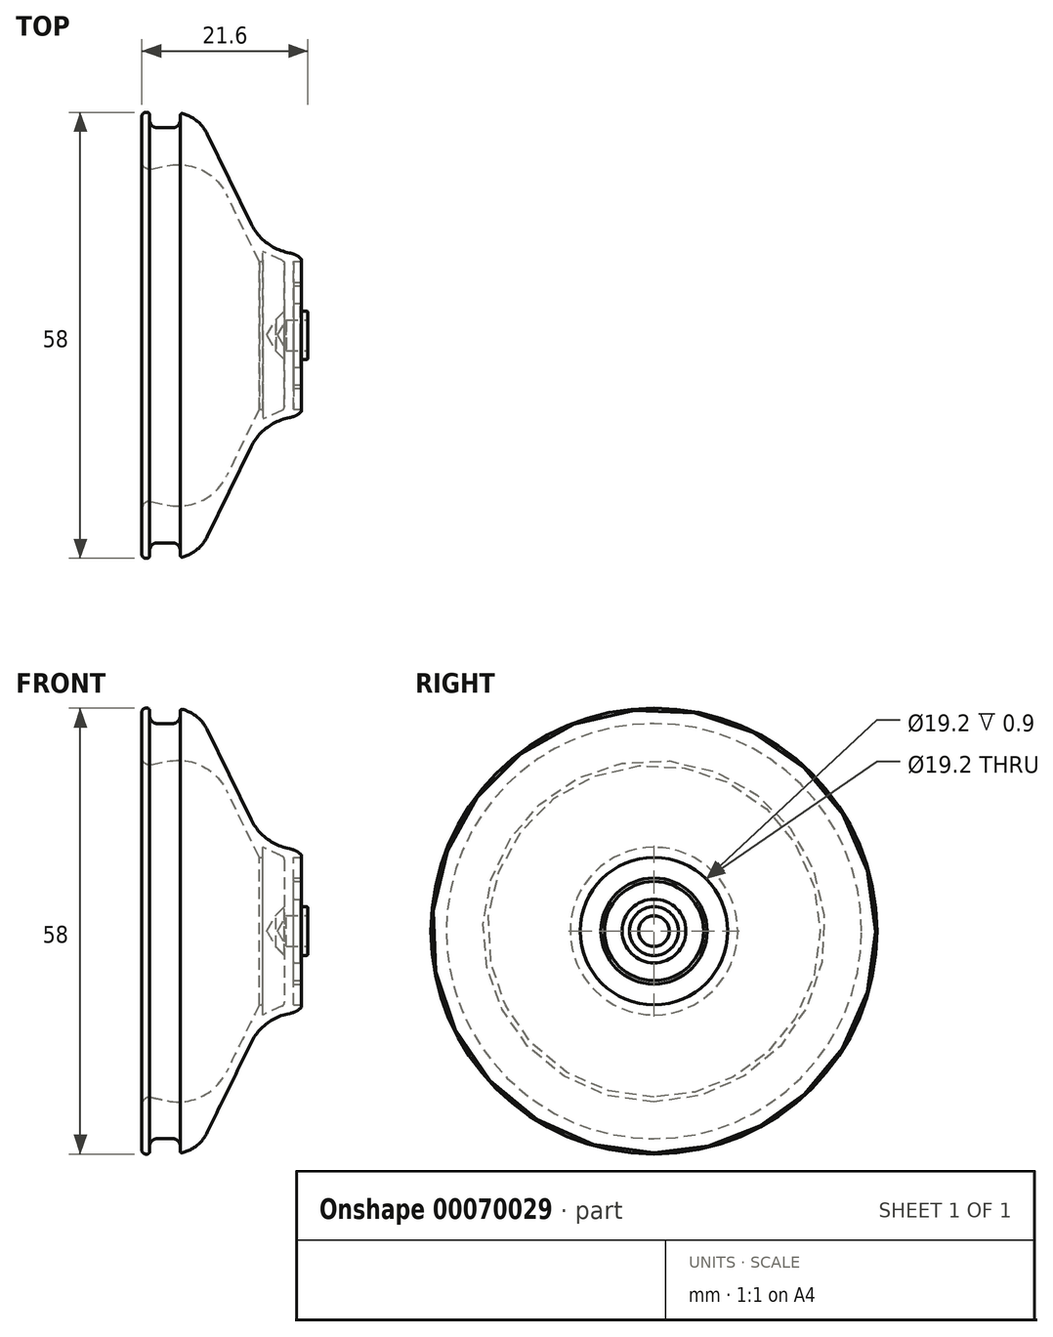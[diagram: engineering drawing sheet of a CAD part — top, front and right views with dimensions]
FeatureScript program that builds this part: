
annotation { "Feature Type Name" : "Feature", "Feature Type Description" : "" }
export const myFeature = defineFeature(function(context is Context, id is Id, definition is map)
    precondition{}
    {
        {
            var Q0;
            Q0=qCreatedBy(makeId("Front.planeOp"),FACE);
            var sketch = newSketch(context, id + "F0", { "sketchPlane" : qUnion([Q0])});
            skLineSegment(sketch, "E0", {"start": v(-1.4, 2) * mm, "end": v(-4.2, 2) * mm});
            skLineSegment(sketch, "E1", {"start": v(-4.2, 2) * mm, "end": v(-5.35, 0) * mm});
            skLineSegment(sketch, "E2", {"start": v(-5.35, 0) * mm, "end": v(-6.74, 0) * mm});
            skLineSegment(sketch, "E3", {"start": v(-6.74, 0) * mm, "end": v(-5.54, 2.08) * mm});
            skLineSegment(sketch, "E4", {"start": v(-7.44, 9.6) * mm, "end": v(-7.74, 9.6) * mm});
            skLineSegment(sketch, "E5", {"start": v(-7.74, 9.6) * mm, "end": v(-11.98, 18.29) * mm});
            skLineSegment(sketch, "E6", {"start": v(-23, 22.6) * mm, "end": v(-23, 29) * mm});
            skLineSegment(sketch, "E7", {"start": v(-23, 29) * mm, "end": v(-22.3, 29) * mm});
            skLineSegment(sketch, "E8", {"start": v(-1.4, 3.17) * mm, "end": v(-2.4, 3.17) * mm});
            skLineSegment(sketch, "E9", {"start": v(-2.4, 3.17) * mm, "end": v(-2.4, 4.15) * mm});
            skLineSegment(sketch, "E10", {"start": v(-2.4, 4.15) * mm, "end": v(-3.25, 4.15) * mm});
            skLineSegment(sketch, "E11", {"start": v(-3.25, 4.15) * mm, "end": v(-3.25, 6.45) * mm});
            skLineSegment(sketch, "E12", {"start": v(-3.25, 6.45) * mm, "end": v(-2.25, 6.45) * mm});
            skLineSegment(sketch, "E13", {"start": v(-2.25, 6.45) * mm, "end": v(-2.25, 6.9) * mm});
            skLineSegment(sketch, "E14", {"start": v(-2.25, 6.9) * mm, "end": v(-3.25, 6.9) * mm});
            skLineSegment(sketch, "E15", {"start": v(-3.25, 6.9) * mm, "end": v(-3.25, 9.6) * mm});
            skLineSegment(sketch, "E16", {"start": v(-3.25, 9.6) * mm, "end": v(-2.25, 9.6) * mm});
            skLineSegment(sketch, "E17", {"start": v(-2.25, 9.6) * mm, "end": v(-2.25, 10.6) * mm});
            skLineSegment(sketch, "E18", {"start": v(-1.4, 3.17) * mm, "end": v(-1.4, 2) * mm});
            skLineSegment(sketch, "E19", {"start": v(-2.25, 10.6) * mm, "end": v(-2.25, 10.6) * mm});
            skLineSegment(sketch, "E20", {"start": v(-4.45, 9.6) * mm, "end": v(-4.45, 3.17) * mm});
            skLineSegment(sketch, "E21", {"start": v(-4.45, 3.17) * mm, "end": v(-5.54, 2.08) * mm});
            skLineSegment(sketch, "E22", {"start": v(-2.25, 10.6) * mm, "end": v(-2.52, 10.6) * mm});
            skLineSegment(sketch, "E23", {"start": v(-14.5, 26.2) * mm, "end": v(-8.81, 14.53) * mm});
            skPoint(sketch, "E24.visualSharp", {"position": v(-6.9, 10.6) * mm});
            skArc(sketch, "E24.filletArc", {"start": v(-8.81, 14.53) * mm, "mid": v(-6.23, 11.66) * mm, "end": v(-2.52, 10.6) * mm});
            skPoint(sketch, "E25.visualSharp", {"position": v(-15.87, 29) * mm});
            skArc(sketch, "E25.filletArc", {"start": v(-14.5, 26.2) * mm, "mid": v(-15.83, 27.87) * mm, "end": v(-17.75, 28.84) * mm});
            skLineSegment(sketch, "E26", {"start": v(-21.8, 21.62) * mm, "end": v(-19.73, 22.06) * mm});
            skPoint(sketch, "E27.visualSharp", {"position": v(-14.38, 23.2) * mm});
            skArc(sketch, "E27.filletArc", {"start": v(-11.98, 18.29) * mm, "mid": v(-15.2, 21.51) * mm, "end": v(-19.73, 22.06) * mm});
            skPoint(sketch, "E28.visualSharp", {"position": v(-23, 21.37) * mm});
            skLineSegment(sketch, "E29", {"start": v(-7.24, 9.8) * mm, "end": v(-7.24, 10.9) * mm});
            skLineSegment(sketch, "E30", {"start": v(-7.24, 10.9) * mm, "end": v(-4.45, 9.6) * mm});
            skPoint(sketch, "E31.visualSharp", {"position": v(-7.24, 9.6) * mm});
            skArc(sketch, "E31.filletArc", {"start": v(-7.44, 9.6) * mm, "mid": v(-7.3, 9.66) * mm, "end": v(-7.24, 9.8) * mm});
            skLineSegment(sketch, "E32", {"start": v(-22, 28.7) * mm, "end": v(-22, 28) * mm});
            skLineSegment(sketch, "E33", {"start": v(-21, 27) * mm, "end": v(-19, 27) * mm});
            skLineSegment(sketch, "E34", {"start": v(-18, 28) * mm, "end": v(-18, 28.65) * mm});
            skPoint(sketch, "E35.visualSharp", {"position": v(-22, 27) * mm});
            skArc(sketch, "E35.filletArc", {"start": v(-22, 28) * mm, "mid": v(-21.7, 27.3) * mm, "end": v(-21, 27) * mm});
            skPoint(sketch, "E36.visualSharp", {"position": v(-18, 27) * mm});
            skArc(sketch, "E36.filletArc", {"start": v(-19, 27) * mm, "mid": v(-18.3, 27.3) * mm, "end": v(-18, 28) * mm});
            skPoint(sketch, "E37.visualSharp", {"position": v(-22, 29) * mm});
            skArc(sketch, "E37.filletArc", {"start": v(-22, 28.7) * mm, "mid": v(-22.09, 28.91) * mm, "end": v(-22.3, 29) * mm});
            skPoint(sketch, "E38.visualSharp", {"position": v(-18, 28.9) * mm});
            skArc(sketch, "E38.filletArc", {"start": v(-17.75, 28.84) * mm, "mid": v(-17.92, 28.8) * mm, "end": v(-18, 28.65) * mm});
            skArc(sketch, "E39.filletArc", {"start": v(-23, 22.6) * mm, "mid": v(-22.63, 21.83) * mm, "end": v(-21.8, 21.62) * mm});
            skSolve(sketch);
        }
        {
            var Q0;
            Q0=qSketchRegion(id+"F0",true);
            var Q1;
            Q1=sQuery(id+"F0.wireOp",EDGE,"E2");
            revolve(context, id + "F1", {"entities" : qUnion([Q0]), "axis" : qUnion([Q1]), "revolveType" : RevolveType.FULL});
        }
        {
            var Q0;
            Q0=makeQuery(id+"F1.opRevolve","SWEPT_EDGE",EDGE,{"disambiguationData":[OSD([sQuery(id+"F0.wireOp",EDGE,"E17"),sQuery(id+"F0.wireOp",EDGE,"E22")])]});
            chamfer(context, id + "F2", {"entities" : qUnion([Q0]), "chamferType" : ChamferType.TWO_OFFSETS, "width1" : 0.7 * mm, "oppositeDirection" : false, "width2" : 0.8 * mm, "tangentPropagation" : true});
        }
        {
            var Q0;
            Q0=makeQuery(id+"F2.opChamfer","BLEND_EDGE",EDGE,{"blendedFrom":[makeQuery(id+"F1.opRevolve","SWEPT_EDGE",EDGE,{"disambiguationData":[OSD([sQuery(id+"F0.wireOp",EDGE,"E17"),sQuery(id+"F0.wireOp",EDGE,"E22")])]}),makeQuery(id+"F1.opRevolve","SWEPT_FACE",FACE,{"disambiguationData":[OSD([sQuery(id+"F0.wireOp",EDGE,"E24.filletArc")])]})],"blendedInto":[makeQuery(id+"F1.opRevolve","SWEPT_FACE",FACE,{"disambiguationData":[OSD([sQuery(id+"F0.wireOp",EDGE,"E24.filletArc")])]})]});
            fillet(context, id + "F3", {"entities" : qUnion([Q0]), "radius" : 3 * mm, "tangentPropagation" : true, "allowEdgeOverflow" : false});
        }
        {
            var Q0;
            {var subQ0=sQuery(id+"F0.wireOp",EDGE,"E17");Q0=makeQuery(id+"F2.opChamfer","BLEND_EDGE",EDGE,{"blendedFrom":[makeQuery(id+"F1.opRevolve","SWEPT_EDGE",EDGE,{"disambiguationData":[OSD([subQ0,sQuery(id+"F0.wireOp",EDGE,"E22")])]}),makeQuery(id+"F1.opRevolve","SWEPT_FACE",FACE,{"disambiguationData":[OSD([subQ0])]})],"blendedInto":[makeQuery(id+"F1.opRevolve","SWEPT_FACE",FACE,{"disambiguationData":[OSD([subQ0])]})]});}
            fillet(context, id + "F4", {"entities" : qUnion([Q0]), "radius" : 0.2 * mm, "tangentPropagation" : true, "allowEdgeOverflow" : false});
        }
        {
            var Q0;
            Q0=makeQuery(id+"F1.opRevolve","SWEPT_EDGE",EDGE,{"disambiguationData":[OSD([sQuery(id+"F0.wireOp",EDGE,"E9"),sQuery(id+"F0.wireOp",EDGE,"E10")])]});
            var Q1;
            Q1=makeQuery(id+"F1.opRevolve","SWEPT_EDGE",EDGE,{"disambiguationData":[OSD([sQuery(id+"F0.wireOp",EDGE,"E10"),sQuery(id+"F0.wireOp",EDGE,"E11")])]});
            var Q2;
            Q2=makeQuery(id+"F1.opRevolve","SWEPT_EDGE",EDGE,{"disambiguationData":[OSD([sQuery(id+"F0.wireOp",EDGE,"E12"),sQuery(id+"F0.wireOp",EDGE,"E13")])]});
            var Q3;
            Q3=makeQuery(id+"F1.opRevolve","SWEPT_EDGE",EDGE,{"disambiguationData":[OSD([sQuery(id+"F0.wireOp",EDGE,"E13"),sQuery(id+"F0.wireOp",EDGE,"E14")])]});
            var Q4;
            Q4=makeQuery(id+"F1.opRevolve","SWEPT_EDGE",EDGE,{"disambiguationData":[OSD([sQuery(id+"F0.wireOp",EDGE,"E16"),sQuery(id+"F0.wireOp",EDGE,"E17")])]});
            var Q5;
            Q5=makeQuery(id+"F1.opRevolve","SWEPT_EDGE",EDGE,{"disambiguationData":[OSD([sQuery(id+"F0.wireOp",EDGE,"E11"),sQuery(id+"F0.wireOp",EDGE,"E12")])]});
            var Q6;
            Q6=makeQuery(id+"F1.opRevolve","SWEPT_EDGE",EDGE,{"disambiguationData":[OSD([sQuery(id+"F0.wireOp",EDGE,"E8"),sQuery(id+"F0.wireOp",EDGE,"E9")])]});
            fillet(context, id + "F5", {"entities" : qUnion([Q0, Q1, Q2, Q3, Q4, Q5, Q6]), "radius" : 0.1 * mm, "tangentPropagation" : true, "allowEdgeOverflow" : false});
        }
        {
            var Q0;
            Q0=makeQuery(id+"F1.opRevolve","SWEPT_EDGE",EDGE,{"disambiguationData":[OSD([sQuery(id+"F0.wireOp",EDGE,"E8"),sQuery(id+"F0.wireOp",EDGE,"E18")])]});
            fillet(context, id + "F6", {"entities" : qUnion([Q0]), "radius" : 0.2 * mm, "tangentPropagation" : true, "allowEdgeOverflow" : false});
        }
        {
            var Q0;
            Q0=makeQuery(id+"F1.opRevolve","SWEPT_EDGE",EDGE,{"disambiguationData":[OSD([sQuery(id+"F0.wireOp",EDGE,"E6"),sQuery(id+"F0.wireOp",EDGE,"E7")])]});
            fillet(context, id + "F7", {"entities" : qUnion([Q0]), "radius" : 0.5 * mm, "tangentPropagation" : true, "allowEdgeOverflow" : false});
        }
        {
            var Q0;
            Q0=makeQuery(id+"F1.opRevolve","SWEPT_EDGE",EDGE,{"disambiguationData":[OSD([sQuery(id+"F0.wireOp",EDGE,"E20"),sQuery(id+"F0.wireOp",EDGE,"E30")])]});
            fillet(context, id + "F8", {"entities" : qUnion([Q0]), "radius" : 0.5 * mm, "tangentPropagation" : true, "allowEdgeOverflow" : false});
        }
    });
